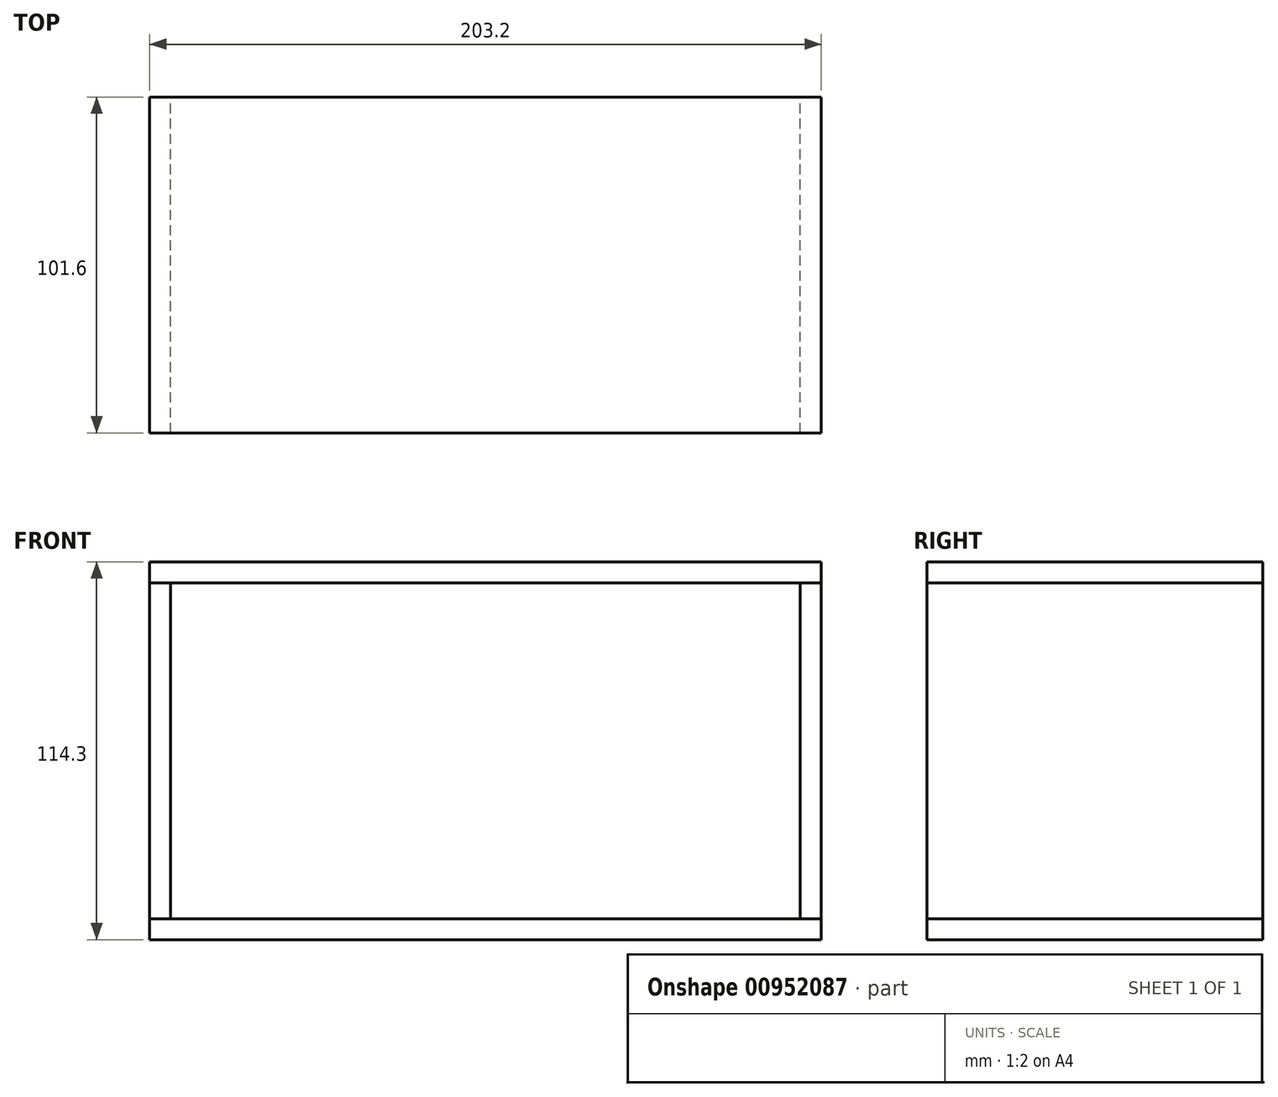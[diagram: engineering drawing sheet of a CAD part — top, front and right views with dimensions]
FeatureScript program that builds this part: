
annotation { "Feature Type Name" : "Feature", "Feature Type Description" : "" }
export const myFeature = defineFeature(function(context is Context, id is Id, definition is map)
    precondition{}
    {
        {
            var Q0;
            Q0=qCreatedBy(makeId("Front.planeOp"),FACE);
            var sketch = newSketch(context, id + "F0", { "sketchPlane" : qUnion([Q0])});
            skLineSegment(sketch, "E0", {"start": v(-101.6, 0) * mm, "end": v(101.6, 0) * mm});
            skLineSegment(sketch, "E1", {"start": v(-101.6, 6.35) * mm, "end": v(101.6, 6.35) * mm});
            skLineSegment(sketch, "E2", {"start": v(-101.6, 6.35) * mm, "end": v(-101.6, 0) * mm});
            skLineSegment(sketch, "E3", {"start": v(101.6, 6.35) * mm, "end": v(101.6, 0) * mm});
            skLineSegment(sketch, "E4", {"start": v(-101.6, 114.3) * mm, "end": v(101.6, 114.3) * mm});
            skLineSegment(sketch, "E5", {"start": v(-101.6, 114.3) * mm, "end": v(-101.6, 6.35) * mm});
            skLineSegment(sketch, "E6", {"start": v(101.6, 114.3) * mm, "end": v(101.6, 6.35) * mm});
            skLineSegment(sketch, "E7", {"start": v(-101.6, 107.95) * mm, "end": v(101.6, 107.95) * mm});
            skLineSegment(sketch, "E8", {"start": v(0, 114.3) * mm, "end": v(0, 107.95) * mm, "construction": true});
            skLineSegment(sketch, "E9", {"start": v(-95.25, 107.95) * mm, "end": v(-95.25, 6.35) * mm});
            skLineSegment(sketch, "E10", {"start": v(95.25, 107.95) * mm, "end": v(95.25, 6.35) * mm});
            skLineSegment(sketch, "E11", {"start": v(-101.6, 57.15) * mm, "end": v(-95.25, 57.15) * mm, "construction": true});
            skLineSegment(sketch, "E12", {"start": v(95.25, 57.15) * mm, "end": v(101.6, 57.15) * mm, "construction": true});
            skLineSegment(sketch, "E13", {"start": v(-95.25, 57.15) * mm, "end": v(95.25, 57.15) * mm});
            skLineSegment(sketch, "E14", {"start": v(-84.13, 72.1) * mm, "end": v(-84.13, 21.3) * mm});
            skLineSegment(sketch, "E15", {"start": v(-84.13, 72.1) * mm, "end": v(-71.43, 72.1) * mm});
            skLineSegment(sketch, "E16", {"start": v(-71.43, 72.1) * mm, "end": v(-71.43, 21.3) * mm});
            skLineSegment(sketch, "E17", {"start": v(-84.13, 21.3) * mm, "end": v(-71.43, 21.3) * mm});
            skSolve(sketch);
        }
        {
            var Q0;
            {var subQ1=sQuery(id+"F0.wireOp",EDGE,"E4");Q0=makeQuery(id+"F0.imprint","IMPRINT",FACE,{"disambiguationData":[TD([[makeQuery(id+"F0.imprint","IMPRINT",EDGE,{"derivedFrom":subQ1}),-1.0]])]});}
            var Q1;
            Q1=makeQuery(id+"F0.imprint","IMPRINT",FACE,{"disambiguationData":[TD([[makeQuery(id+"F0.imprint","IMPRINT",EDGE,{"derivedFrom":sQuery(id+"F0.wireOp",EDGE,"E0")}),1.0]])]});
            extrude(context, id + "F1", {"entities" : qUnion([Q0, Q1]), "endBound" : BoundingType.SYMMETRIC, "depth" : 101.6 * mm, "offsetDistance" : 25.4 * mm});
        }
        {
            var Q0;
            {var subQ1=sQuery(id+"F0.wireOp",EDGE,"E7");var subQ4=sQuery(id+"F0.wireOp",EDGE,"E5");var subQ7=makeQuery(id+"F0.imprint","INTERSECT",VERTEX,{"derivedFrom":[subQ4,subQ1]});Q0=makeQuery(id+"F0.imprint","IMPRINT",FACE,{"disambiguationData":[TD([[makeQuery(id+"F0.imprint","IMPRINT",EDGE,{"disambiguationData":[TD([[subQ7,-1.0]])],"derivedFrom":subQ1}),-1.0]])]});}
            var Q1;
            {var subQ1=sQuery(id+"F0.wireOp",EDGE,"E7");var subQ4=sQuery(id+"F0.wireOp",EDGE,"E6");var subQ7=makeQuery(id+"F0.imprint","INTERSECT",VERTEX,{"derivedFrom":[subQ4,subQ1]});Q1=makeQuery(id+"F0.imprint","IMPRINT",FACE,{"disambiguationData":[TD([[makeQuery(id+"F0.imprint","IMPRINT",EDGE,{"disambiguationData":[TD([[subQ7,1.0]])],"derivedFrom":subQ1}),-1.0]])]});}
            var Q2;
            Q2=makeQuery(id+"F1.opExtrude","CAP_FACE",FACE,{"disambiguationData":[OSD([sQuery(id+"F0.wireOp",EDGE,"E4"),sQuery(id+"F0.wireOp",EDGE,"E5"),sQuery(id+"F0.wireOp",EDGE,"E6"),sQuery(id+"F0.wireOp",EDGE,"E7")])],"isStart":false});
            var Q3;
            Q3=makeQuery(id+"F1.opExtrude","CAP_FACE",FACE,{"disambiguationData":[OSD([sQuery(id+"F0.wireOp",EDGE,"E4"),sQuery(id+"F0.wireOp",EDGE,"E5"),sQuery(id+"F0.wireOp",EDGE,"E6"),sQuery(id+"F0.wireOp",EDGE,"E7")])],"isStart":true});
            extrude(context, id + "F2", {"entities" : qUnion([Q0, Q1]), "endBound" : BoundingType.UP_TO_SURFACE, "depth" : 25.4 * mm, "endBoundEntityFace" : qUnion([Q2]), "offsetDistance" : 25.4 * mm, "hasSecondDirection" : true, "secondDirectionBound" : SecondDirectionBoundingType.UP_TO_SURFACE, "secondDirectionOppositeDirection" : true, "secondDirectionDepth" : 25.4 * mm, "secondDirectionBoundEntityFace" : qUnion([Q3])});
        }
    });
